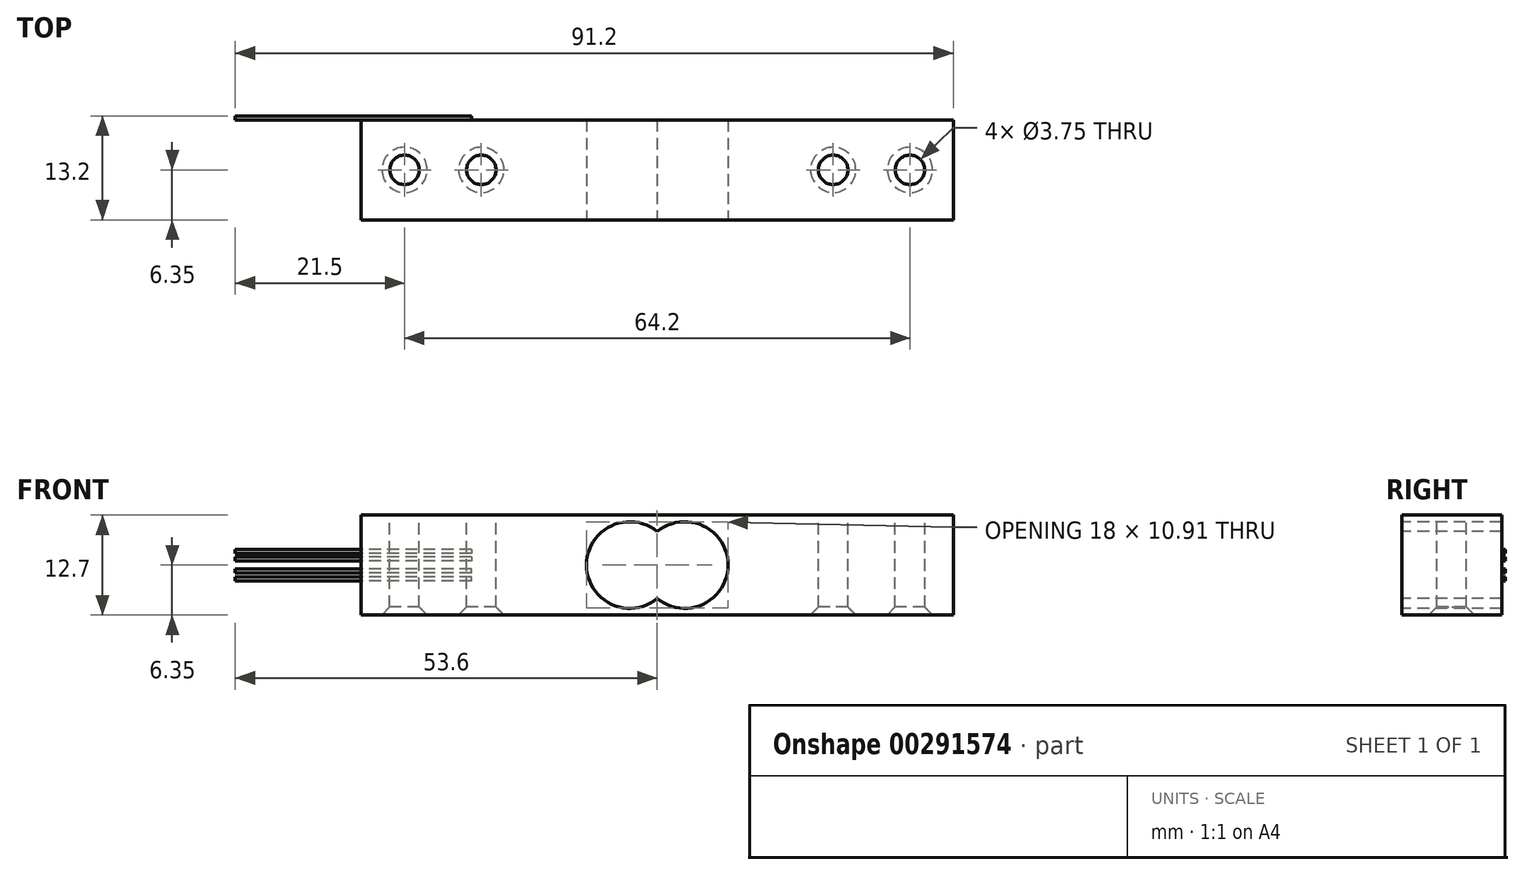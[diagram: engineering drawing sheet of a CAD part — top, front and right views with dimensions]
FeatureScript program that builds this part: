
annotation { "Feature Type Name" : "Feature", "Feature Type Description" : "" }
export const myFeature = defineFeature(function(context is Context, id is Id, definition is map)
    precondition{}
    {
        {
            var Q0;
            Q0=qCreatedBy(makeId("Top.planeOp"),FACE);
            var sketch = newSketch(context, id + "F0", { "sketchPlane" : qUnion([Q0])});
            skLineSegment(sketch, "E0.bottom", {"start": v(37.6, -6.35) * mm, "end": v(-37.6, -6.35) * mm});
            skLineSegment(sketch, "E0.top", {"start": v(37.6, 6.35) * mm, "end": v(-37.6, 6.35) * mm});
            skLineSegment(sketch, "E0.left", {"start": v(37.6, -6.35) * mm, "end": v(37.6, 6.35) * mm});
            skLineSegment(sketch, "E0.right", {"start": v(-37.6, -6.35) * mm, "end": v(-37.6, 6.35) * mm});
            skPoint(sketch, "E0.middle", {"position": v(0, 0) * mm});
            skSolve(sketch);
        }
        {
            var Q0;
            Q0 = qSketchRegion(id + "F0", true);
            extrude(context, id + "F1", {"entities" : qUnion([Q0]), "depth" : (12.7 / 2) * mm, "hasSecondDirection" : true, "secondDirectionOppositeDirection" : true, "secondDirectionDepth" : 6.35 * mm});
        }
        {
            var Q0;
            Q0=makeQuery(id+"F1.opExtrude","SWEPT_FACE",FACE,{"disambiguationData":[OSD([sQuery(id+"F0.wireOp",EDGE,"E0.bottom")])]});
            var sketch = newSketch(context, id + "F2", { "sketchPlane" : qUnion([Q0])});
            skLineSegment(sketch, "E1", {"start": v(0, 22.65) * mm, "end": v(0, -18.02) * mm, "construction": true});
            skPoint(sketch, "E1.endSnap0", {"position": v(0, -6.35) * mm});
            skLineSegment(sketch, "E2", {"start": v(-24.04, 0) * mm, "end": v(29.61, 0) * mm, "construction": true});
            skArc(sketch, "E3", {"start": v(0, -4.24) * mm, "mid": v(9, 0) * mm, "end": v(0, 4.24) * mm});
            skLineSegment(sketch, "E4", {"start": v(9, 14.04) * mm, "end": v(9, -17.62) * mm, "construction": true});
            skArc(sketch, "E5.MirrorCS", {"start": v(0, -4.24) * mm, "mid": v(-9, 0) * mm, "end": v(0, 4.24) * mm});
            skSolve(sketch);
        }
        {
            var Q0;
            Q0 = qSketchRegion(id + "F2", true);
            extrude(context, id + "F3", {"entities" : qUnion([Q0]), "operationType" : NewBodyOperationType.REMOVE, "oppositeDirection" : true, "depth" : 25 * mm});
        }
        {
            var Q0;
            Q0=makeQuery(id+"F1.opExtrude","SWEPT_FACE",FACE,{"disambiguationData":[OSD([sQuery(id+"F0.wireOp",EDGE,"E0.top")])]});
            var sketch = newSketch(context, id + "F4", { "sketchPlane" : qUnion([Q0])});
            skLineSegment(sketch, "E6", {"start": v(23.6, 18.33) * mm, "end": v(23.6, -21.01) * mm, "construction": true});
            skLineSegment(sketch, "E7.bottom", {"start": v(23.6, 2) * mm, "end": v(53.6, 2) * mm});
            skLineSegment(sketch, "E7.top", {"start": v(23.6, 1.5) * mm, "end": v(53.6, 1.5) * mm});
            skLineSegment(sketch, "E7.left", {"start": v(23.6, 2) * mm, "end": v(23.6, 1.5) * mm});
            skLineSegment(sketch, "E7.right", {"start": v(53.6, 2) * mm, "end": v(53.6, 1.5) * mm});
            skLineSegment(sketch, "E8.0.1.0", {"start": v(23.6, 0.5) * mm, "end": v(53.6, 0.5) * mm});
            skLineSegment(sketch, "E8.0.1.1", {"start": v(23.6, 1) * mm, "end": v(53.6, 1) * mm});
            skLineSegment(sketch, "E8.0.1.2", {"start": v(53.6, 1) * mm, "end": v(53.6, 0.5) * mm});
            skLineSegment(sketch, "E8.0.1.3", {"start": v(23.6, 1) * mm, "end": v(23.6, 0.5) * mm});
            skLineSegment(sketch, "E8.direction1", {"start": v(23.6, 1.5) * mm, "end": v(48.6, 1.5) * mm, "construction": true});
            skLineSegment(sketch, "E8.direction2", {"start": v(23.6, 1.5) * mm, "end": v(23.6, 0.5) * mm, "construction": true});
            skLineSegment(sketch, "E9.MirrorCS", {"start": v(23.6, -1.5) * mm, "end": v(48.6, -1.5) * mm, "construction": true});
            skLineSegment(sketch, "E10.MirrorCS", {"start": v(23.6, -1.5) * mm, "end": v(23.6, -0.5) * mm, "construction": true});
            skLineSegment(sketch, "E11.MirrorCS", {"start": v(23.6, -1) * mm, "end": v(23.6, -0.5) * mm});
            skLineSegment(sketch, "E12.MirrorCS", {"start": v(53.6, -1) * mm, "end": v(53.6, -0.5) * mm});
            skLineSegment(sketch, "E13.MirrorCS", {"start": v(23.6, -2) * mm, "end": v(23.6, -1.5) * mm});
            skLineSegment(sketch, "E14.MirrorCS", {"start": v(53.6, -2) * mm, "end": v(53.6, -1.5) * mm});
            skLineSegment(sketch, "E15.MirrorCS", {"start": v(23.6, -0.5) * mm, "end": v(53.6, -0.5) * mm});
            skLineSegment(sketch, "E16.MirrorCS", {"start": v(23.6, -1) * mm, "end": v(53.6, -1) * mm});
            skLineSegment(sketch, "E17.MirrorCS", {"start": v(23.6, -2) * mm, "end": v(53.6, -2) * mm});
            skLineSegment(sketch, "E18.MirrorCS", {"start": v(23.6, -1.5) * mm, "end": v(53.6, -1.5) * mm});
            skSolve(sketch);
        }
        {
            var Q0;
            Q0 = qSketchRegion(id + "F4", true);
            extrude(context, id + "F5", {"entities" : qUnion([Q0]), "operationType" : NewBodyOperationType.ADD, "depth" : 0.5 * mm});
        }
        {
            var Q0;
            Q0=makeQuery(id+"F1.opExtrude","CAP_FACE",FACE,{"disambiguationData":[OSD([sQuery(id+"F0.wireOp",EDGE,"E0.bottom"),sQuery(id+"F0.wireOp",EDGE,"E0.top"),sQuery(id+"F0.wireOp",EDGE,"E0.left"),sQuery(id+"F0.wireOp",EDGE,"E0.right")])],"isStart":false});
            var sketch = newSketch(context, id + "F6", { "sketchPlane" : qUnion([Q0])});
            skCircle(sketch, "E19", {"center": v(32.1, 0) * mm, "radius": 1.88 * mm});
            skCircle(sketch, "E20", {"center": v(22.35, 0) * mm, "radius": 1.88 * mm});
            skCircle(sketch, "E21.MirrorC", {"center": v(-22.35, 0) * mm, "radius": 1.88 * mm});
            skCircle(sketch, "E22.MirrorC", {"center": v(-32.1, 0) * mm, "radius": 1.88 * mm});
            skSolve(sketch);
        }
        {
            var Q0;
            Q0 = qSketchRegion(id + "F6", true);
            extrude(context, id + "F7", {"entities" : qUnion([Q0]), "operationType" : NewBodyOperationType.REMOVE, "oppositeDirection" : true, "depth" : 25 * mm});
        }
        {
            var Q0;
            Q0=makeQuery(id+"F7.boolean.opBoolean","COPY",EDGE,{"derivedFrom":makeQuery(id+"F7.opExtrude","CAP_EDGE",EDGE,{"disambiguationData":[OSD([sQuery(id+"F6.wireOp",EDGE,"E19")])],"isStart":true})});
            var Q1;
            Q1=makeQuery(id+"F7.boolean.opBoolean","COPY",EDGE,{"derivedFrom":makeQuery(id+"F7.opExtrude","CAP_EDGE",EDGE,{"disambiguationData":[OSD([sQuery(id+"F6.wireOp",EDGE,"E20")])],"isStart":true})});
            var Q2;
            Q2=makeQuery(id+"F7.boolean.opBoolean","COPY",EDGE,{"derivedFrom":makeQuery(id+"F7.opExtrude","CAP_EDGE",EDGE,{"disambiguationData":[OSD([sQuery(id+"F6.wireOp",EDGE,"E21.MirrorC")])],"isStart":true})});
            var Q3;
            Q3=makeQuery(id+"F7.boolean.opBoolean","COPY",EDGE,{"derivedFrom":makeQuery(id+"F7.opExtrude","CAP_EDGE",EDGE,{"disambiguationData":[OSD([sQuery(id+"F6.wireOp",EDGE,"E22.MirrorC")])],"isStart":true})});
            var Q4;
            Q4=makeQuery(id+"F7.boolean.opBoolean","INTERSECT",EDGE,{"derivedFrom":[makeQuery(id+"F1.opExtrude","CAP_FACE",FACE,{"disambiguationData":[OSD([sQuery(id+"F0.wireOp",EDGE,"E0.bottom"),sQuery(id+"F0.wireOp",EDGE,"E0.top"),sQuery(id+"F0.wireOp",EDGE,"E0.left"),sQuery(id+"F0.wireOp",EDGE,"E0.right")])],"isStart":true}),makeQuery(id+"F7.opExtrude","SWEPT_FACE",FACE,{"disambiguationData":[OSD([sQuery(id+"F6.wireOp",EDGE,"E22.MirrorC")])]})]});
            var Q5;
            Q5=makeQuery(id+"F7.boolean.opBoolean","INTERSECT",EDGE,{"derivedFrom":[makeQuery(id+"F1.opExtrude","CAP_FACE",FACE,{"disambiguationData":[OSD([sQuery(id+"F0.wireOp",EDGE,"E0.bottom"),sQuery(id+"F0.wireOp",EDGE,"E0.top"),sQuery(id+"F0.wireOp",EDGE,"E0.left"),sQuery(id+"F0.wireOp",EDGE,"E0.right")])],"isStart":true}),makeQuery(id+"F7.opExtrude","SWEPT_FACE",FACE,{"disambiguationData":[OSD([sQuery(id+"F6.wireOp",EDGE,"E21.MirrorC")])]})]});
            var Q6;
            Q6=makeQuery(id+"F7.boolean.opBoolean","INTERSECT",EDGE,{"derivedFrom":[makeQuery(id+"F1.opExtrude","CAP_FACE",FACE,{"disambiguationData":[OSD([sQuery(id+"F0.wireOp",EDGE,"E0.bottom"),sQuery(id+"F0.wireOp",EDGE,"E0.top"),sQuery(id+"F0.wireOp",EDGE,"E0.left"),sQuery(id+"F0.wireOp",EDGE,"E0.right")])],"isStart":true}),makeQuery(id+"F7.opExtrude","SWEPT_FACE",FACE,{"disambiguationData":[OSD([sQuery(id+"F6.wireOp",EDGE,"E20")])]})]});
            var Q7;
            Q7=makeQuery(id+"F7.boolean.opBoolean","INTERSECT",EDGE,{"derivedFrom":[makeQuery(id+"F1.opExtrude","CAP_FACE",FACE,{"disambiguationData":[OSD([sQuery(id+"F0.wireOp",EDGE,"E0.bottom"),sQuery(id+"F0.wireOp",EDGE,"E0.top"),sQuery(id+"F0.wireOp",EDGE,"E0.left"),sQuery(id+"F0.wireOp",EDGE,"E0.right")])],"isStart":true}),makeQuery(id+"F7.opExtrude","SWEPT_FACE",FACE,{"disambiguationData":[OSD([sQuery(id+"F6.wireOp",EDGE,"E19")])]})]});
            chamfer(context, id + "F8", {"entities" : qUnion([Q0, Q1, Q2, Q3, Q4, Q5, Q6, Q7]), "width" : 1 * mm, "tangentPropagation" : true});
        }
    });
